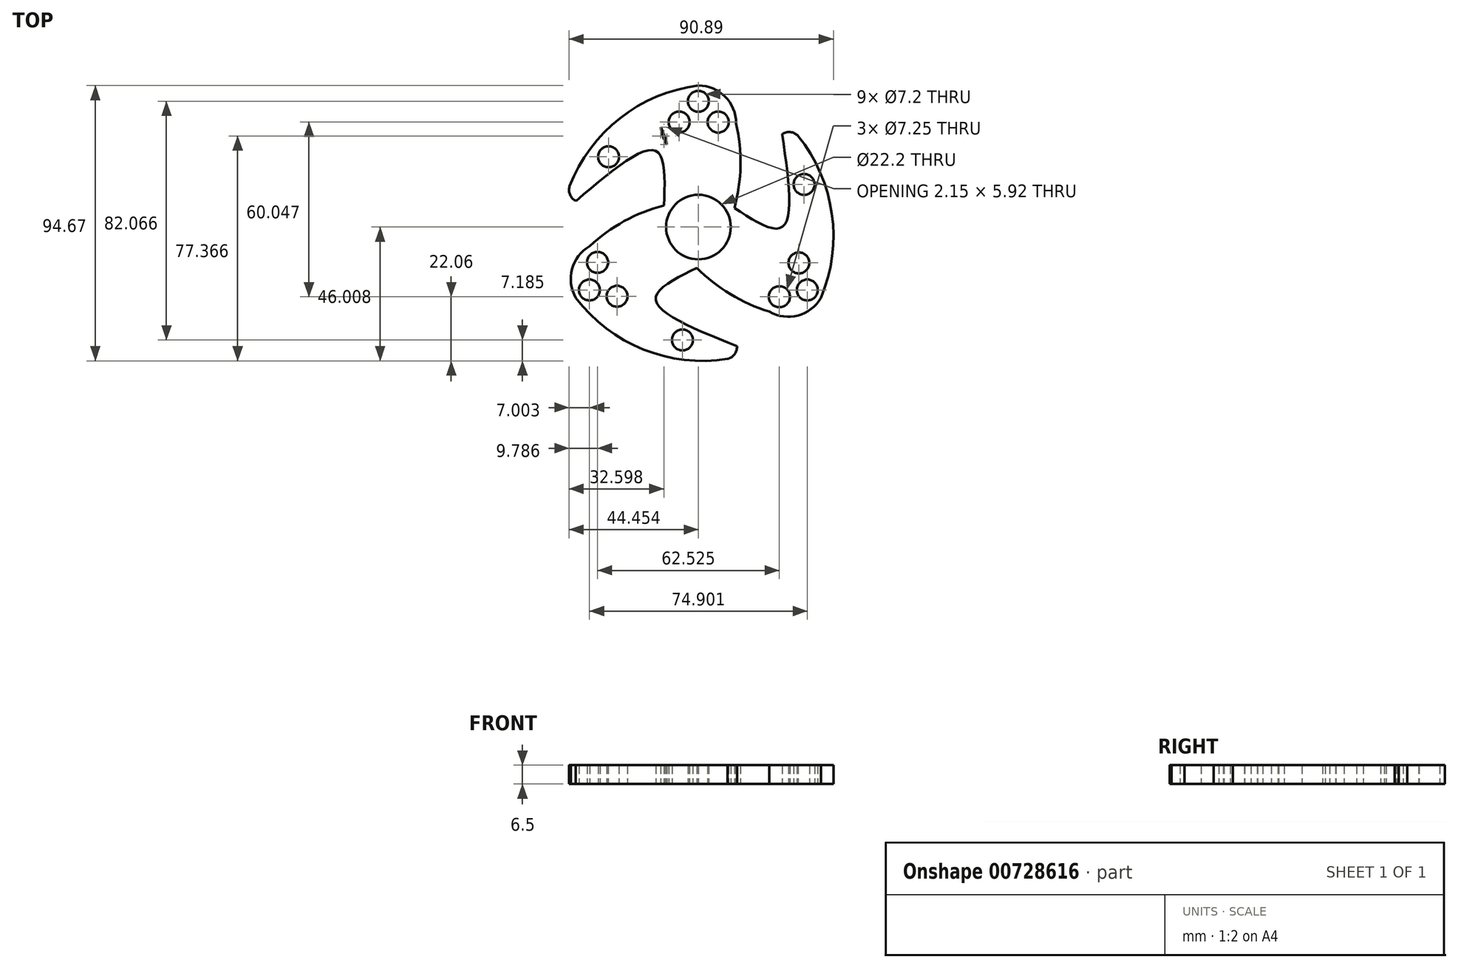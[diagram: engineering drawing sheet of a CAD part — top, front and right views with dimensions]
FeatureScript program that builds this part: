
annotation { "Feature Type Name" : "Feature", "Feature Type Description" : "" }
export const myFeature = defineFeature(function(context is Context, id is Id, definition is map)
    precondition{}
    {
        {
            var Q0;
            Q0=qCreatedBy(makeId("Top.planeOp"),FACE);
            var sketch = newSketch(context, id + "F0", { "sketchPlane" : qUnion([Q0])});
            skCircle(sketch, "E0", {"center": v(0.13, -0.01) * mm, "radius": 11.1 * mm});
            skCircle(sketch, "E1", {"center": v(0.13, -0.01) * mm, "radius": 14 * mm});
            skCircle(sketch, "E2", {"center": v(0.13, 35.65) * mm, "radius": 13 * mm});
            skArc(sketch, "E3", {"start": v(-13.35, 3.75) * mm, "mid": v(-9.52, 18.96) * mm, "end": v(-12.8, 34.3) * mm});
            skCircle(sketch, "E4.1.2", {"center": v(-30.75, -17.84) * mm, "radius": 13 * mm});
            skArc(sketch, "E4.1.3", {"start": v(3.62, -13.57) * mm, "mid": v(-11.48, -17.86) * mm, "end": v(-23.12, -28.37) * mm});
            skCircle(sketch, "E4.2.2", {"center": v(31.02, -17.84) * mm, "radius": 13 * mm});
            skArc(sketch, "E4.2.3", {"start": v(10.14, 9.78) * mm, "mid": v(21.4, -1.14) * mm, "end": v(36.32, -5.97) * mm});
            skArc(sketch, "E5", {"start": v(0.13, 48.65) * mm, "mid": v(-26.8, 37.43) * mm, "end": v(-44.14, 13.97) * mm});
            skArc(sketch, "E6.1.0", {"start": v(-42, -24.34) * mm, "mid": v(-18.83, -42.06) * mm, "end": v(10.16, -45.35) * mm});
            skArc(sketch, "E6.2.0", {"start": v(42.28, -24.34) * mm, "mid": v(46.03, 4.6) * mm, "end": v(34.38, 31.34) * mm});
            skArc(sketch, "E7", {"start": v(12.52, 6.52) * mm, "mid": v(14.63, 21.04) * mm, "end": v(13.13, 35.65) * mm});
            skArc(sketch, "E8.1.0", {"start": v(-11.71, 7.45) * mm, "mid": v(-25.35, 2.01) * mm, "end": v(-37.25, -6.58) * mm});
            skArc(sketch, "E8.2.0", {"start": v(-0.4, -14) * mm, "mid": v(11.12, -23.1) * mm, "end": v(24.52, -29.1) * mm});
            skCircle(sketch, "E9", {"center": v(-6.48, 36.09) * mm, "radius": 3.6 * mm});
            skCircle(sketch, "E10", {"center": v(0.13, 43.23) * mm, "radius": 3.6 * mm});
            skCircle(sketch, "E11", {"center": v(6.94, 36.09) * mm, "radius": 3.62 * mm});
            skCircle(sketch, "E12", {"center": v(-30.75, 24.14) * mm, "radius": 3.6 * mm});
            skCircle(sketch, "E13.1.0", {"center": v(-5.34, -38.83) * mm, "radius": 3.6 * mm});
            skCircle(sketch, "E13.1.1", {"center": v(-27.82, -23.79) * mm, "radius": 3.6 * mm});
            skCircle(sketch, "E13.1.2", {"center": v(-37.32, -21.63) * mm, "radius": 3.6 * mm});
            skCircle(sketch, "E13.1.3", {"center": v(-34.53, -12.16) * mm, "radius": 3.62 * mm});
            skCircle(sketch, "E13.2.0", {"center": v(36.5, 14.66) * mm, "radius": 3.6 * mm});
            skCircle(sketch, "E13.2.1", {"center": v(34.7, -12.34) * mm, "radius": 3.6 * mm});
            skCircle(sketch, "E13.2.2", {"center": v(37.58, -21.63) * mm, "radius": 3.6 * mm});
            skCircle(sketch, "E13.2.3", {"center": v(28, -23.96) * mm, "radius": 3.62 * mm});
            skArc(sketch, "E14", {"start": v(34.38, 31.34) * mm, "mid": v(31.78, 32.64) * mm, "end": v(28.96, 31.95) * mm});
            skArc(sketch, "E15.1.0", {"start": v(-44.14, 13.97) * mm, "mid": v(-43.97, 11.07) * mm, "end": v(-41.96, 8.96) * mm});
            skArc(sketch, "E15.2.0", {"start": v(10.16, -45.35) * mm, "mid": v(12.6, -43.75) * mm, "end": v(13.4, -40.96) * mm});
            skFitSpline(sketch, "E16", {"points": [v(28.96, 31.95) * mm, v(28.96, 0) * mm, v(12.52, 6.52) * mm], "startDerivative": vector(11.05, -76.08) * mm, "endDerivative": vector(-46.75, 30.42) * mm});
            skFitSpline(sketch, "E17", {"points": [v(-41.96, 8.96) * mm, v(-14.52, 26.2) * mm, v(-11.71, 7.45) * mm], "startDerivative": vector(60.31, 51.27) * mm, "endDerivative": vector(-2.61, -59.21) * mm});
            skFitSpline(sketch, "E18", {"points": [v(13.4, -40.96) * mm, v(-14.52, -24.88) * mm, v(-0.4, -14) * mm], "startDerivative": vector(-72.15, 28.76) * mm, "endDerivative": vector(50.54, 24.97) * mm});
            skSolve(sketch);
        }
        {
            var Q0;
            Q0=makeQuery(id+"F0.imprint","IMPRINT",FACE,{"disambiguationData":[TD([[makeQuery(id+"F0.imprint","IMPRINT",EDGE,{"derivedFrom":sQuery(id+"F0.wireOp",EDGE,"E12")}),-1.0]])]});
            var Q1;
            {var subQ0=sQuery(id+"F0.wireOp",EDGE,"E3");var subQ1=sQuery(id+"F0.wireOp",EDGE,"E2");var subQ2=makeQuery(id+"F0.imprint","INTERSECT",VERTEX,{"disambiguationData":[OD(0.0)],"derivedFrom":[subQ1,subQ0]});Q1=makeQuery(id+"F0.imprint","IMPRINT",FACE,{"disambiguationData":[TD([[makeQuery(id+"F0.imprint","IMPRINT",EDGE,{"disambiguationData":[TD([[subQ2,-1.0]])],"derivedFrom":subQ1}),1.0]])]});}
            var Q2;
            {var subQ0=sQuery(id+"F0.wireOp",EDGE,"E4.2.3");var subQ1=sQuery(id+"F0.wireOp",EDGE,"E1");var subQ2=makeQuery(id+"F0.imprint","INTERSECT",VERTEX,{"derivedFrom":[subQ1,subQ0]});Q2=makeQuery(id+"F0.imprint","IMPRINT",FACE,{"disambiguationData":[TD([[makeQuery(id+"F0.imprint","IMPRINT",EDGE,{"disambiguationData":[TD([[subQ2,1.0]])],"derivedFrom":subQ1}),1.0]])]});}
            var Q3;
            {var subQ0=sQuery(id+"F0.wireOp",EDGE,"E4.2.3");var subQ1=sQuery(id+"F0.wireOp",EDGE,"E4.2.2");var subQ2=makeQuery(id+"F0.imprint","INTERSECT",VERTEX,{"disambiguationData":[OD(0.0)],"derivedFrom":[subQ1,subQ0]});Q3=makeQuery(id+"F0.imprint","IMPRINT",FACE,{"disambiguationData":[TD([[makeQuery(id+"F0.imprint","IMPRINT",EDGE,{"disambiguationData":[TD([[subQ2,-1.0]])],"derivedFrom":subQ1}),1.0]])]});}
            var Q4;
            {var subQ0=sQuery(id+"F0.wireOp",EDGE,"E3");var subQ1=sQuery(id+"F0.wireOp",EDGE,"E1");var subQ2=makeQuery(id+"F0.imprint","INTERSECT",VERTEX,{"derivedFrom":[subQ1,subQ0]});Q4=makeQuery(id+"F0.imprint","IMPRINT",FACE,{"disambiguationData":[TD([[makeQuery(id+"F0.imprint","IMPRINT",EDGE,{"disambiguationData":[TD([[subQ2,1.0]])],"derivedFrom":subQ1}),1.0]])]});}
            var Q5;
            {var subQ5=sQuery(id+"F0.wireOp",EDGE,"E8.2.0");Q5=makeQuery(id+"F0.imprint","IMPRINT",FACE,{"disambiguationData":[TD([[makeQuery(id+"F0.imprint","IMPRINT",EDGE,{"derivedFrom":subQ5}),1.0]])]});}
            var Q6;
            {var subQ0=sQuery(id+"F0.wireOp",EDGE,"E4.1.3");var subQ1=sQuery(id+"F0.wireOp",EDGE,"E1");var subQ2=makeQuery(id+"F0.imprint","INTERSECT",VERTEX,{"derivedFrom":[subQ1,subQ0]});Q6=makeQuery(id+"F0.imprint","IMPRINT",FACE,{"disambiguationData":[TD([[makeQuery(id+"F0.imprint","IMPRINT",EDGE,{"disambiguationData":[TD([[subQ2,1.0]])],"derivedFrom":subQ1}),1.0]])]});}
            var Q7;
            {var subQ0=sQuery(id+"F0.wireOp",EDGE,"E4.1.3");var subQ1=sQuery(id+"F0.wireOp",EDGE,"E4.1.2");var subQ2=makeQuery(id+"F0.imprint","INTERSECT",VERTEX,{"disambiguationData":[OD(0.0)],"derivedFrom":[subQ1,subQ0]});Q7=makeQuery(id+"F0.imprint","IMPRINT",FACE,{"disambiguationData":[TD([[makeQuery(id+"F0.imprint","IMPRINT",EDGE,{"disambiguationData":[TD([[subQ2,-1.0]])],"derivedFrom":subQ1}),1.0]])]});}
            var Q8;
            Q8=makeQuery(id+"F0.imprint","IMPRINT",FACE,{"disambiguationData":[TD([[makeQuery(id+"F0.imprint","IMPRINT",EDGE,{"derivedFrom":sQuery(id+"F0.wireOp",EDGE,"E13.1.1")}),-1.0]])]});
            var Q9;
            {var subQ5=sQuery(id+"F0.wireOp",EDGE,"E8.1.0");Q9=makeQuery(id+"F0.imprint","IMPRINT",FACE,{"disambiguationData":[TD([[makeQuery(id+"F0.imprint","IMPRINT",EDGE,{"derivedFrom":subQ5}),1.0]])]});}
            var Q10;
            Q10=makeQuery(id+"F0.imprint","IMPRINT",FACE,{"disambiguationData":[TD([[makeQuery(id+"F0.imprint","IMPRINT",EDGE,{"derivedFrom":sQuery(id+"F0.wireOp",EDGE,"E0")}),-1.0]])]});
            var Q11;
            {var subQ7=sQuery(id+"F0.wireOp",EDGE,"E7");Q11=makeQuery(id+"F0.imprint","IMPRINT",FACE,{"disambiguationData":[TD([[makeQuery(id+"F0.imprint","IMPRINT",EDGE,{"derivedFrom":subQ7}),1.0]])]});}
            var Q12;
            Q12=makeQuery(id+"F0.imprint","IMPRINT",FACE,{"disambiguationData":[TD([[makeQuery(id+"F0.imprint","IMPRINT",EDGE,{"derivedFrom":sQuery(id+"F0.wireOp",EDGE,"E9")}),-1.0]])]});
            var Q13;
            Q13=makeQuery(id+"F0.imprint","IMPRINT",FACE,{"disambiguationData":[TD([[makeQuery(id+"F0.imprint","IMPRINT",EDGE,{"derivedFrom":sQuery(id+"F0.wireOp",EDGE,"E13.2.0")}),-1.0]])]});
            var Q14;
            Q14=makeQuery(id+"F0.imprint","IMPRINT",FACE,{"disambiguationData":[TD([[makeQuery(id+"F0.imprint","IMPRINT",EDGE,{"derivedFrom":sQuery(id+"F0.wireOp",EDGE,"E13.2.1")}),-1.0]])]});
            var Q15;
            Q15=makeQuery(id+"F0.imprint","IMPRINT",FACE,{"disambiguationData":[TD([[makeQuery(id+"F0.imprint","IMPRINT",EDGE,{"derivedFrom":sQuery(id+"F0.wireOp",EDGE,"E13.1.0")}),-1.0]])]});
            extrude(context, id + "F1", {"entities" : qUnion([Q0, Q1, Q2, Q3, Q4, Q5, Q6, Q7, Q8, Q9, Q10, Q11, Q12, Q13, Q14, Q15]), "depth" : 6.5 * mm, "offsetDistance" : 25 * mm});
        }
    });
